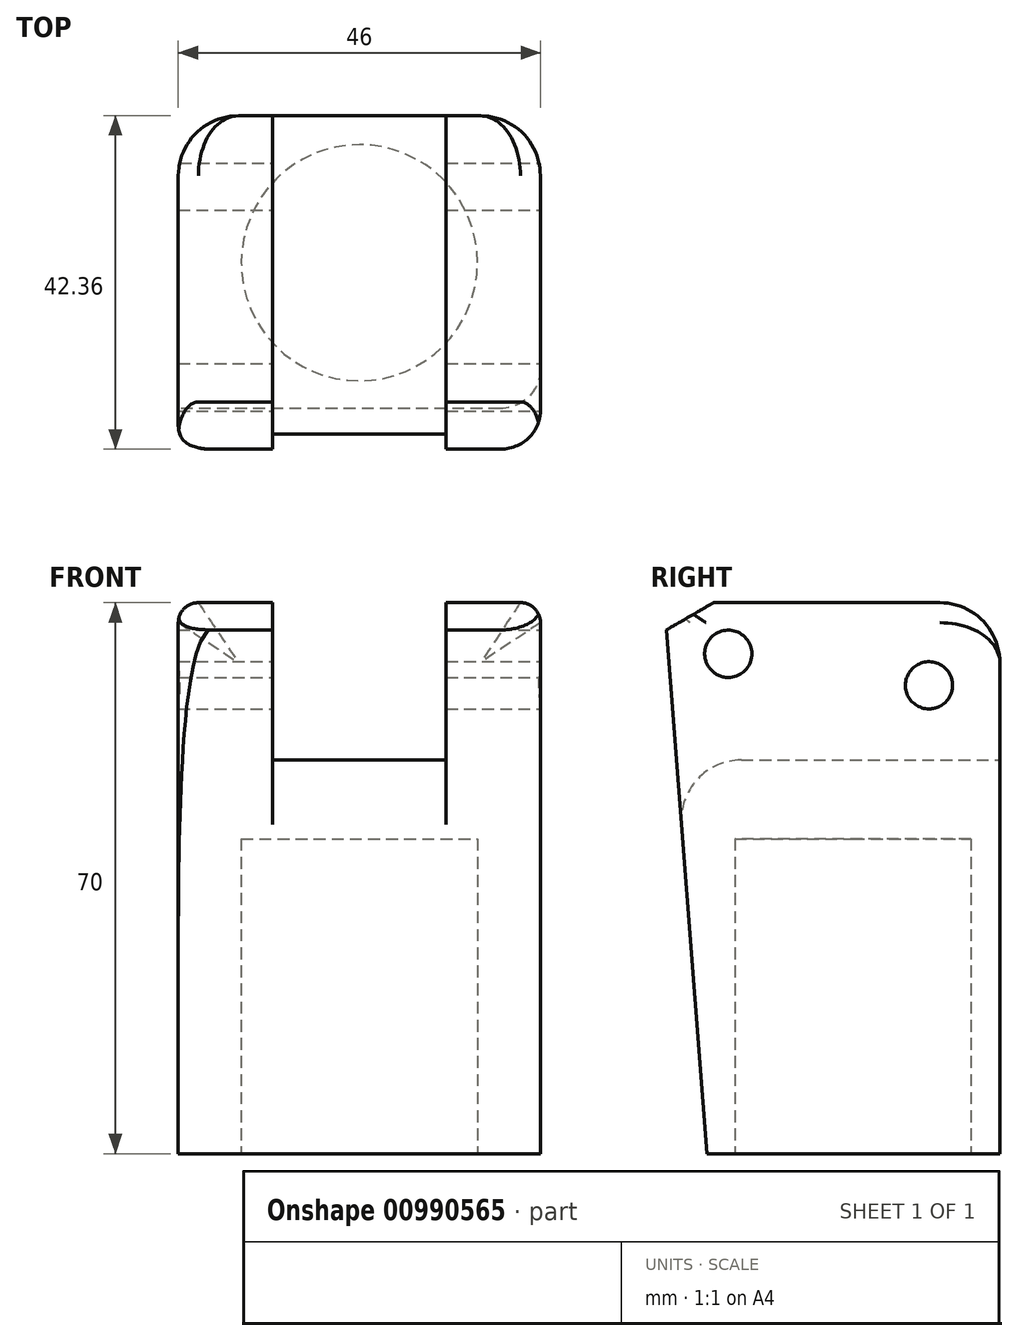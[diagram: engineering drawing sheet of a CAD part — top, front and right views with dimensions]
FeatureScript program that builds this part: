
annotation { "Feature Type Name" : "Feature", "Feature Type Description" : "" }
export const myFeature = defineFeature(function(context is Context, id is Id, definition is map)
    precondition{}
    {
        {
            var Q0;
            Q0=qCreatedBy(makeId("Right.planeOp"),FACE);
            var sketch = newSketch(context, id + "F0", { "sketchPlane" : qUnion([Q0])});
            skLineSegment(sketch, "E0", {"start": v(0, 0) * mm, "end": v(52, 0) * mm});
            skLineSegment(sketch, "E1", {"start": v(52, 0) * mm, "end": v(52, -70) * mm});
            skLineSegment(sketch, "E2", {"start": v(12, -60) * mm, "end": v(0, 0) * mm});
            skLineSegment(sketch, "E3", {"start": v(52, -70) * mm, "end": v(12, -70) * mm});
            skLineSegment(sketch, "E4", {"start": v(12, -70) * mm, "end": v(12, -60) * mm});
            skSolve(sketch);
        }
        {
            var Q0;
            Q0=makeQuery(id+"F0.imprint","IMPRINT",FACE,{"disambiguationData":[TD([[makeQuery(id+"F0.imprint","IMPRINT",EDGE,{"derivedFrom":sQuery(id+"F0.wireOp",EDGE,"E0")}),-1.0]])]});
            extrude(context, id + "F1", {"entities" : qUnion([Q0]), "depth" : 46 * mm, "offsetDistance" : 25.4 * mm});
        }
        {
            var Q0;
            Q0=makeQuery(id+"F1.opExtrude","SWEPT_FACE",FACE,{"disambiguationData":[OSD([sQuery(id+"F0.wireOp",EDGE,"E3")])]});
            var sketch = newSketch(context, id + "F2", { "sketchPlane" : qUnion([Q0])});
            skCircle(sketch, "E5", {"center": v(23, -33.32) * mm, "radius": 15 * mm});
            skLineSegment(sketch, "E6", {"start": v(23, -33.32) * mm, "end": v(46, -33.32) * mm});
            skLineSegment(sketch, "E7", {"start": v(23, -33.32) * mm, "end": v(23, -52) * mm});
            skSolve(sketch);
        }
        {
            var Q0;
            {var subQ0=sQuery(id+"F2.wireOp",EDGE,"E6");var subQ1=sQuery(id+"F2.wireOp",EDGE,"E5");var subQ2=makeQuery(id+"F2.imprint","INTERSECT",VERTEX,{"derivedFrom":[subQ1,subQ0]});Q0=makeQuery(id+"F2.imprint","IMPRINT",FACE,{"disambiguationData":[TD([[makeQuery(id+"F2.imprint","IMPRINT",EDGE,{"disambiguationData":[TD([[subQ2,-1.0]])],"derivedFrom":subQ1}),1.0]])]});}
            var Q1;
            {var subQ0=sQuery(id+"F2.wireOp",EDGE,"E6");var subQ1=sQuery(id+"F2.wireOp",EDGE,"E5");var subQ2=makeQuery(id+"F2.imprint","INTERSECT",VERTEX,{"derivedFrom":[subQ1,subQ0]});Q1=makeQuery(id+"F2.imprint","IMPRINT",FACE,{"disambiguationData":[TD([[makeQuery(id+"F2.imprint","IMPRINT",EDGE,{"disambiguationData":[TD([[subQ2,1.0]])],"derivedFrom":subQ1}),1.0]])]});}
            extrude(context, id + "F3", {"entities" : qUnion([Q0, Q1]), "operationType" : NewBodyOperationType.REMOVE, "oppositeDirection" : true, "depth" : 40 * mm, "offsetDistance" : 25.4 * mm});
        }
        {
            var Q0;
            Q0=makeQuery(id+"F1.opExtrude","CAP_FACE",FACE,{"disambiguationData":[OSD([sQuery(id+"F0.wireOp",EDGE,"E0"),sQuery(id+"F0.wireOp",EDGE,"E1"),sQuery(id+"F0.wireOp",EDGE,"E2"),sQuery(id+"F0.wireOp",EDGE,"E3"),sQuery(id+"F0.wireOp",EDGE,"E4")])],"isStart":false});
            var sketch = newSketch(context, id + "F4", { "sketchPlane" : qUnion([Q0])});
            skCircle(sketch, "E8", {"center": v(43, -10.5) * mm, "radius": 3 * mm});
            skCircle(sketch, "E9", {"center": v(17.5, -6.5) * mm, "radius": 3 * mm});
            skLineSegment(sketch, "E10", {"start": v(43, -10.5) * mm, "end": v(43, 0) * mm});
            skLineSegment(sketch, "E11", {"start": v(17.5, -6.5) * mm, "end": v(52, -6.5) * mm});
            skLineSegment(sketch, "E12", {"start": v(17.5, -6.5) * mm, "end": v(17.5, 0) * mm});
            skSolve(sketch);
        }
        {
            var Q0;
            Q0=makeQuery(id+"F4.imprint","IMPRINT",FACE,{"disambiguationData":[TD([[makeQuery(id+"F4.imprint","IMPRINT",EDGE,{"derivedFrom":sQuery(id+"F4.wireOp",EDGE,"E9")}),1.0]])]});
            extrude(context, id + "F5", {"entities" : qUnion([Q0]), "operationType" : NewBodyOperationType.REMOVE, "oppositeDirection" : true, "depth" : 254 * mm, "offsetDistance" : 25.4 * mm});
        }
        {
            var Q0;
            Q0=makeQuery(id+"F1.opExtrude","SWEPT_FACE",FACE,{"disambiguationData":[OSD([sQuery(id+"F0.wireOp",EDGE,"E1")])]});
            var sketch = newSketch(context, id + "F6", { "sketchPlane" : qUnion([Q0])});
            skLineSegment(sketch, "E13", {"start": v(-34, 0) * mm, "end": v(-34, -20) * mm});
            skLineSegment(sketch, "E14", {"start": v(-34, -20) * mm, "end": v(-12, -20) * mm});
            skLineSegment(sketch, "E15", {"start": v(-12, -20) * mm, "end": v(-12, 0) * mm});
            skSolve(sketch);
        }
        {
            var Q0;
            {var subQ0=sQuery(id+"F6.wireOp",EDGE,"E13");Q0=makeQuery(id+"F6.imprint","IMPRINT",FACE,{"disambiguationData":[TD([[makeQuery(id+"F6.imprint","IMPRINT",EDGE,{"derivedFrom":subQ0}),1.0]])]});}
            extrude(context, id + "F7", {"entities" : qUnion([Q0]), "operationType" : NewBodyOperationType.REMOVE, "oppositeDirection" : true, "depth" : 1346.2 * mm, "offsetDistance" : 25.4 * mm});
        }
        {
            var Q0;
            Q0=makeQuery(id+"F4.imprint","IMPRINT",FACE,{"disambiguationData":[TD([[makeQuery(id+"F4.imprint","IMPRINT",EDGE,{"derivedFrom":sQuery(id+"F4.wireOp",EDGE,"E8")}),1.0]])]});
            extrude(context, id + "F8", {"entities" : qUnion([Q0]), "operationType" : NewBodyOperationType.REMOVE, "oppositeDirection" : true, "depth" : 65 * mm, "offsetDistance" : 25.4 * mm});
        }
        {
            var Q0;
            Q0=makeQuery(id+"F4.imprint","IMPRINT",FACE,{"disambiguationData":[TD([[makeQuery(id+"F4.imprint","IMPRINT",EDGE,{"derivedFrom":sQuery(id+"F4.wireOp",EDGE,"E8")}),-1.0]])]});
            var sketch = newSketch(context, id + "F9", { "sketchPlane" : qUnion([Q0])});
            skLineSegment(sketch, "E16", {"start": v(1.63, -8.1) * mm, "end": v(15.64, 0) * mm});
            skLineSegment(sketch, "E17", {"start": v(15.64, 0) * mm, "end": v(0, 0) * mm});
            skLineSegment(sketch, "E18", {"start": v(0, 0) * mm, "end": v(1.14, -8.1) * mm});
            skLineSegment(sketch, "E19", {"start": v(1.14, -8.1) * mm, "end": v(1.63, -8.1) * mm});
            skSolve(sketch);
        }
        {
            var Q0;
            Q0 = qSketchRegion(id + "F9", true);
            extrude(context, id + "F10", {"entities" : qUnion([Q0]), "operationType" : NewBodyOperationType.REMOVE, "oppositeDirection" : true, "depth" : 127 * mm, "offsetDistance" : 25.4 * mm});
        }
        {
            var Q0;
            Q0=qCreatedBy(makeId("Right.planeOp"),FACE);
            var sketch = newSketch(context, id + "F11", { "sketchPlane" : qUnion([Q0])});
            skLineSegment(sketch, "E20", {"start": v(14.8, -70.08) * mm, "end": v(9.37, 0) * mm});
            skLineSegment(sketch, "E21", {"start": v(9.37, 0) * mm, "end": v(0, 0) * mm});
            skLineSegment(sketch, "E22", {"start": v(0, 0) * mm, "end": v(0, -70.36) * mm});
            skLineSegment(sketch, "E23", {"start": v(0, -70.36) * mm, "end": v(14.8, -70.08) * mm});
            skLineSegment(sketch, "E24", {"start": v(48.57, 0) * mm, "end": v(48.57, -70.46) * mm});
            skLineSegment(sketch, "E25", {"start": v(48.57, -70.46) * mm, "end": v(52.07, -70.46) * mm});
            skLineSegment(sketch, "E26", {"start": v(52.07, -70.46) * mm, "end": v(52.07, 0) * mm});
            skLineSegment(sketch, "E27", {"start": v(52.07, 0) * mm, "end": v(48.57, 0) * mm});
            skSolve(sketch);
        }
        {
            var Q0;
            Q0=makeQuery(id+"F11.imprint","IMPRINT",FACE,{"disambiguationData":[TD([[makeQuery(id+"F11.imprint","IMPRINT",EDGE,{"derivedFrom":sQuery(id+"F11.wireOp",EDGE,"E20")}),1.0]])]});
            extrude(context, id + "F12", {"entities" : qUnion([Q0]), "operationType" : NewBodyOperationType.REMOVE, "depth" : 254 * mm, "offsetDistance" : 25.4 * mm});
        }
        {
            var Q0;
            {var subQ2=sQuery(id+"F0.wireOp",EDGE,"E0");Q0=makeQuery(id+"F7.boolean.opBoolean","SPLIT",FACE,{"disambiguationData":[TD([makeQuery(id+"F7.opExtrude","SWEPT_FACE",FACE,{"disambiguationData":[OSD([sQuery(id+"F6.wireOp",EDGE,"E15")])]})])],"derivedFrom":makeQuery(id+"F1.opExtrude","SWEPT_FACE",FACE,{"disambiguationData":[OSD([subQ2])]})});}
            var sketch = newSketch(context, id + "F13", { "sketchPlane" : qUnion([Q0])});
            skFitSpline(sketch, "E28", {"points": [v(0, 12.66) * mm, v(3.92, 9.63) * mm], "startDerivative": vector(0, -8.14) * mm, "endDerivative": vector(3.97, -0.35) * mm});
            skLineSegment(sketch, "E29", {"start": v(0, 12.66) * mm, "end": v(0, 9.54) * mm});
            skLineSegment(sketch, "E30", {"start": v(0, 9.54) * mm, "end": v(3.92, 9.63) * mm});
            skFitSpline(sketch, "E31.MirrorCS", {"points": [v(46, 12.66) * mm, v(42.08, 9.63) * mm], "startDerivative": vector(0, -8.14) * mm, "endDerivative": vector(-3.97, -0.35) * mm});
            skLineSegment(sketch, "E32.MirrorCS", {"start": v(46, 9.54) * mm, "end": v(42.08, 9.63) * mm});
            skLineSegment(sketch, "E33.MirrorCS", {"start": v(46, 12.66) * mm, "end": v(46, 9.54) * mm});
            skSolve(sketch);
        }
        {
            var Q0;
            Q0 = qSketchRegion(id + "F13", true);
            extrude(context, id + "F14", {"entities" : qUnion([Q0]), "operationType" : NewBodyOperationType.REMOVE, "oppositeDirection" : true, "depth" : 254 * mm, "offsetDistance" : 25.4 * mm});
        }
        {
            var Q0;
            Q0=makeQuery(id+"F12.boolean.opBoolean","COPY",EDGE,{"derivedFrom":makeQuery(id+"F12.opExtrude","CAP_EDGE",EDGE,{"disambiguationData":[OSD([sQuery(id+"F11.wireOp",EDGE,"E20")])],"isStart":true})});
            var Q1;
            Q1=makeQuery(id+"F12.boolean.opBoolean","INTERSECT",EDGE,{"derivedFrom":[makeQuery(id+"F1.opExtrude","CAP_FACE",FACE,{"disambiguationData":[OSD([sQuery(id+"F0.wireOp",EDGE,"E0"),sQuery(id+"F0.wireOp",EDGE,"E1"),sQuery(id+"F0.wireOp",EDGE,"E2"),sQuery(id+"F0.wireOp",EDGE,"E3"),sQuery(id+"F0.wireOp",EDGE,"E4")])],"isStart":false}),makeQuery(id+"F12.opExtrude","SWEPT_FACE",FACE,{"disambiguationData":[OSD([sQuery(id+"F11.wireOp",EDGE,"E20")])]})]});
            fillet(context, id + "F15", {"entities" : qUnion([Q0, Q1]), "radius" : 5.08 * mm, "tangentPropagation" : true, "allowEdgeOverflow" : false});
        }
        {
            var Q0;
            {var subQ0=sQuery(id+"F0.wireOp",EDGE,"E0");var subQ1=sQuery(id+"F0.wireOp",EDGE,"E1");Q0=makeQuery(id+"F7.boolean.opBoolean","SPLIT",EDGE,{"disambiguationData":[TD([makeQuery(id+"F7.opExtrude","SWEPT_FACE",FACE,{"disambiguationData":[OSD([sQuery(id+"F6.wireOp",EDGE,"E15")])]})])],"derivedFrom":makeQuery(id+"F1.opExtrude","SWEPT_EDGE",EDGE,{"disambiguationData":[OSD([subQ0,subQ1])]})});}
            var Q1;
            {var subQ0=sQuery(id+"F0.wireOp",EDGE,"E0");var subQ1=sQuery(id+"F0.wireOp",EDGE,"E1");Q1=makeQuery(id+"F7.boolean.opBoolean","SPLIT",EDGE,{"disambiguationData":[TD([makeQuery(id+"F7.opExtrude","SWEPT_FACE",FACE,{"disambiguationData":[OSD([sQuery(id+"F6.wireOp",EDGE,"E13")])]})])],"derivedFrom":makeQuery(id+"F1.opExtrude","SWEPT_EDGE",EDGE,{"disambiguationData":[OSD([subQ0,subQ1])]})});}
            var Q2;
            Q2=makeQuery(id+"F1.opExtrude","CAP_EDGE",EDGE,{"disambiguationData":[OSD([sQuery(id+"F0.wireOp",EDGE,"E1")])],"isStart":false});
            var Q3;
            Q3=makeQuery(id+"F1.opExtrude","CAP_EDGE",EDGE,{"disambiguationData":[OSD([sQuery(id+"F0.wireOp",EDGE,"E1")])],"isStart":true});
            var Q4;
            Q4=makeQuery(id+"F7.boolean.opBoolean","COPY",EDGE,{"derivedFrom":makeQuery(id+"F7.opExtrude","SWEPT_EDGE",EDGE,{"disambiguationData":[OSD([sQuery(id+"F0.wireOp",EDGE,"E0"),sQuery(id+"F0.wireOp",EDGE,"E1"),sQuery(id+"F6.wireOp",EDGE,"E13")])]})});
            var Q5;
            Q5=makeQuery(id+"F7.boolean.opBoolean","COPY",EDGE,{"derivedFrom":makeQuery(id+"F7.opExtrude","SWEPT_EDGE",EDGE,{"disambiguationData":[OSD([sQuery(id+"F0.wireOp",EDGE,"E0"),sQuery(id+"F0.wireOp",EDGE,"E1"),sQuery(id+"F6.wireOp",EDGE,"E15")])]})});
            var Q6;
            Q6=makeQuery(id+"F7.boolean.opBoolean","COPY",EDGE,{"derivedFrom":makeQuery(id+"F7.opExtrude","CAP_EDGE",EDGE,{"disambiguationData":[OSD([sQuery(id+"F6.wireOp",EDGE,"E13")])],"isStart":true})});
            var Q7;
            Q7=makeQuery(id+"F7.boolean.opBoolean","COPY",EDGE,{"derivedFrom":makeQuery(id+"F7.opExtrude","CAP_EDGE",EDGE,{"disambiguationData":[OSD([sQuery(id+"F6.wireOp",EDGE,"E14")])],"isStart":true})});
            var Q8;
            Q8=makeQuery(id+"F7.boolean.opBoolean","COPY",EDGE,{"derivedFrom":makeQuery(id+"F7.opExtrude","CAP_EDGE",EDGE,{"disambiguationData":[OSD([sQuery(id+"F6.wireOp",EDGE,"E15")])],"isStart":true})});
            var Q9;
            Q9=makeQuery(id+"F12.boolean.opBoolean","INTERSECT",EDGE,{"derivedFrom":[makeQuery(id+"F7.boolean.opBoolean","COPY",FACE,{"derivedFrom":makeQuery(id+"F7.opExtrude","SWEPT_FACE",FACE,{"disambiguationData":[OSD([sQuery(id+"F6.wireOp",EDGE,"E14")])]})}),makeQuery(id+"F12.opExtrude","SWEPT_FACE",FACE,{"disambiguationData":[OSD([sQuery(id+"F11.wireOp",EDGE,"E20")])]})]});
            fillet(context, id + "F16", {"entities" : qUnion([Q0, Q1, Q2, Q3, Q4, Q5, Q6, Q7, Q8, Q9]), "radius" : 7.62 * mm, "tangentPropagation" : true, "allowEdgeOverflow" : false});
        }
        {
            var Q0;
            Q0=makeQuery(id+"F1.opExtrude","CAP_EDGE",EDGE,{"disambiguationData":[OSD([sQuery(id+"F0.wireOp",EDGE,"E0")])],"isStart":true});
            var Q1;
            Q1=makeQuery(id+"F1.opExtrude","CAP_EDGE",EDGE,{"disambiguationData":[OSD([sQuery(id+"F0.wireOp",EDGE,"E0")])],"isStart":false});
            fillet(context, id + "F17", {"entities" : qUnion([Q0, Q1]), "radius" : 2.54 * mm, "tangentPropagation" : true, "allowEdgeOverflow" : false});
        }
    });
